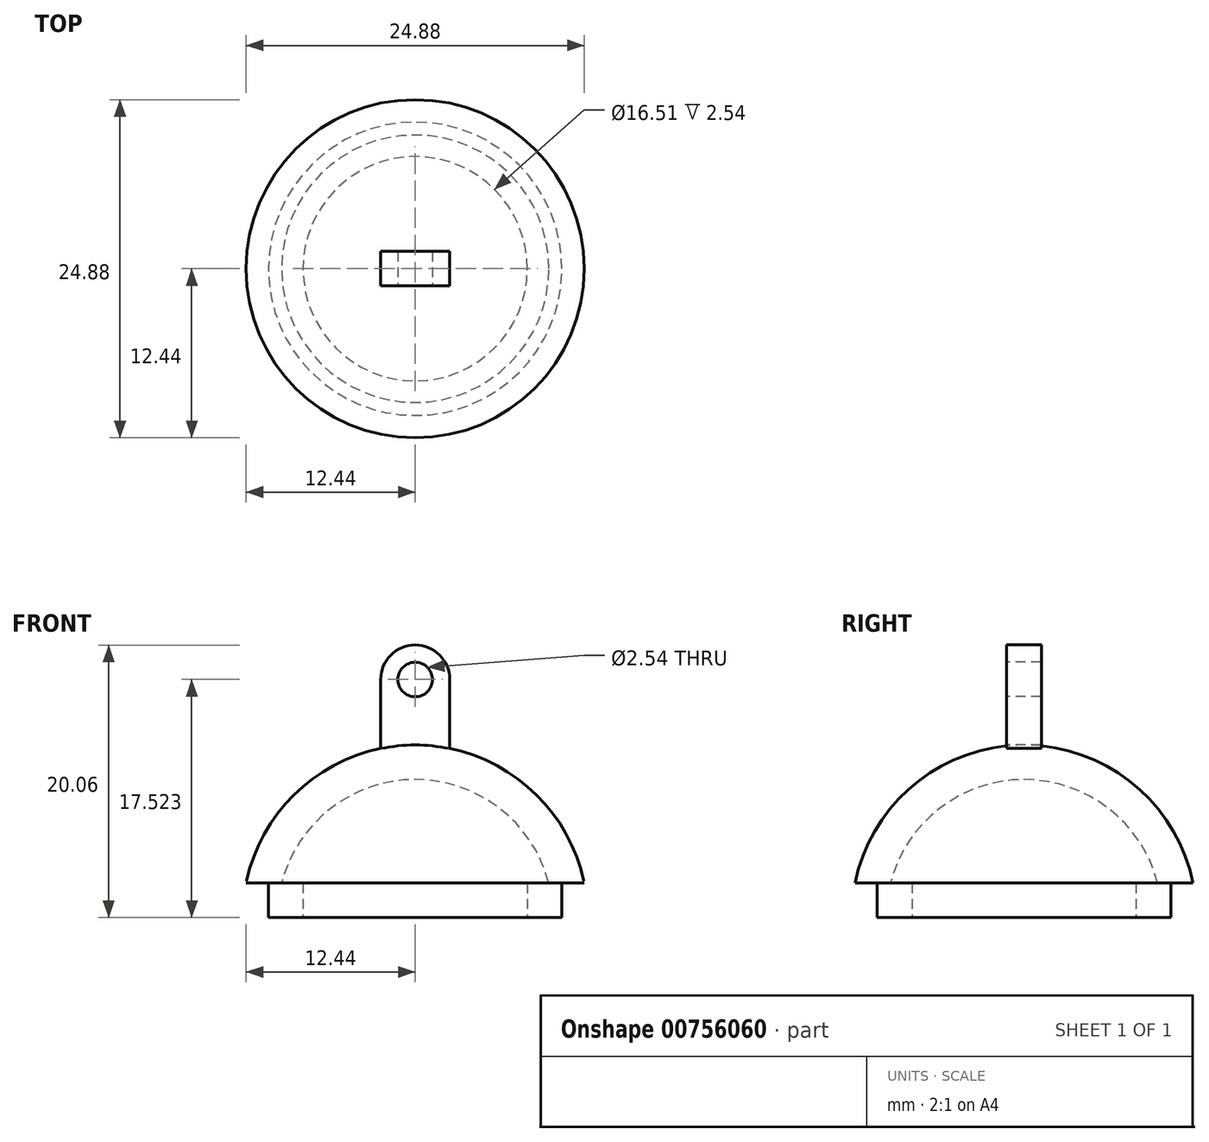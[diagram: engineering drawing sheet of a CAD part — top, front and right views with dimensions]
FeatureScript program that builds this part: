
annotation { "Feature Type Name" : "Feature", "Feature Type Description" : "" }
export const myFeature = defineFeature(function(context is Context, id is Id, definition is map)
    precondition{}
    {
        {
            var Q0;
            Q0=qCreatedBy(makeId("Top.planeOp"),FACE);
            var sketch = newSketch(context, id + "F0", { "sketchPlane" : qUnion([Q0])});
            skArc(sketch, "E0", {"start": v(12.7, 0) * mm, "mid": v(0, 12.7) * mm, "end": v(-12.7, 0) * mm});
            skLineSegment(sketch, "E1", {"start": v(-12.7, 0) * mm, "end": v(12.7, 0) * mm});
            skSolve(sketch);
        }
        {
            var Q0;
            Q0=makeQuery(id+"F0.imprint","IMPRINT",FACE,{"disambiguationData":[TD([[makeQuery(id+"F0.imprint","IMPRINT",EDGE,{"derivedFrom":sQuery(id+"F0.wireOp",EDGE,"E0")}),1.0]])]});
            var Q1;
            Q1=sQuery(id+"F0.wireOp",EDGE,"E1");
            revolve(context, id + "F1", {"surfaceOperationType" : NewSurfaceOperationType.NEW, "entities" : qUnion([Q0]), "axis" : qUnion([Q1]), "revolveType" : RevolveType.ONE_DIRECTION, "angle" : 180 * degree});
        }
        {
            var Q0;
            Q0=makeQuery(id+"F1.opRevolve","CAP_FACE",FACE,{"disambiguationData":[OSD([sQuery(id+"F0.wireOp",EDGE,"E0"),sQuery(id+"F0.wireOp",EDGE,"E1")])],"isStart":true});
            var sketch = newSketch(context, id + "F2", { "sketchPlane" : qUnion([Q0])});
            skCircle(sketch, "E2", {"center": v(0, 0) * mm, "radius": 12.7 * mm});
            skCircle(sketch, "E3", {"center": v(0, 0) * mm, "radius": 10.8 * mm});
            skSolve(sketch);
        }
        {
            var Q0;
            Q0=makeQuery(id+"F2.imprint","IMPRINT",FACE,{"disambiguationData":[TD([[makeQuery(id+"F2.imprint","IMPRINT",EDGE,{"derivedFrom":sQuery(id+"F2.wireOp",EDGE,"E2")}),1.0]])]});
            extrude(context, id + "F3", {"entities" : qUnion([Q0]), "operationType" : NewBodyOperationType.REMOVE, "oppositeDirection" : true, "depth" : 2.54 * mm, "offsetDistance" : 25.4 * mm});
        }
        {
            var Q0;
            Q0=makeQuery(id+"F3.boolean.opBoolean","COPY",FACE,{"derivedFrom":makeQuery(id+"F3.opExtrude","CAP_FACE",FACE,{"disambiguationData":[OSD([sQuery(id+"F2.wireOp",EDGE,"E2")])],"isStart":false})});
            var Q1;
            Q1=makeQuery(id+"F1.opRevolve","CAP_FACE",FACE,{"disambiguationData":[OSD([sQuery(id+"F0.wireOp",EDGE,"E0"),sQuery(id+"F0.wireOp",EDGE,"E1")])],"isStart":true});
            shell(context, id + "F4", {"entities" : qUnion([Q0, Q1]), "thickness" : 2.54 * mm});
        }
        {
            var Q0;
            Q0=qCreatedBy(makeId("Front.planeOp"),FACE);
            var sketch = newSketch(context, id + "F5", { "sketchPlane" : qUnion([Q0])});
            skLineSegment(sketch, "E4", {"start": v(-2.54, 12.44) * mm, "end": v(-2.54, 17.52) * mm});
            skLineSegment(sketch, "E5", {"start": v(2.54, 12.44) * mm, "end": v(2.54, 17.52) * mm});
            skArc(sketch, "E6", {"start": v(2.54, 12.44) * mm, "mid": v(0, 12.7) * mm, "end": v(-2.54, 12.44) * mm});
            skArc(sketch, "E7", {"start": v(2.54, 17.52) * mm, "mid": v(0, 20.06) * mm, "end": v(-2.54, 17.52) * mm});
            skCircle(sketch, "E8", {"center": v(0, 17.52) * mm, "radius": 1.27 * mm});
            skSolve(sketch);
        }
        {
            var Q0;
            Q0=makeQuery(id+"F5.imprint","IMPRINT",FACE,{"disambiguationData":[TD([[makeQuery(id+"F5.imprint","IMPRINT",EDGE,{"derivedFrom":sQuery(id+"F5.wireOp",EDGE,"E4")}),-1.0]])]});
            extrude(context, id + "F6", {"entities" : qUnion([Q0]), "oppositeDirection" : true, "depth" : 1.27 * mm, "offsetDistance" : 25.4 * mm});
        }
        {
            var Q0;
            Q0=qCreatedBy(makeId("Front.planeOp"),FACE);
            var sketch = newSketch(context, id + "F7", { "sketchPlane" : qUnion([Q0])});
            skArc(sketch, "E9", {"start": v(2.54, 12.44) * mm, "mid": v(0, 12.7) * mm, "end": v(-2.54, 12.44) * mm});
            skLineSegment(sketch, "E10", {"start": v(-2.54, 12.44) * mm, "end": v(-2.54, 17.52) * mm});
            skLineSegment(sketch, "E11", {"start": v(2.54, 12.44) * mm, "end": v(2.54, 17.52) * mm});
            skArc(sketch, "E12", {"start": v(2.54, 17.52) * mm, "mid": v(0, 20.06) * mm, "end": v(-2.54, 17.52) * mm});
            skCircle(sketch, "E13", {"center": v(0, 17.52) * mm, "radius": 1.27 * mm});
            skSolve(sketch);
        }
        {
            var Q0;
            Q0=makeQuery(id+"F7.imprint","IMPRINT",FACE,{"disambiguationData":[TD([[makeQuery(id+"F7.imprint","IMPRINT",EDGE,{"derivedFrom":sQuery(id+"F7.wireOp",EDGE,"E9")}),-1.0]])]});
            extrude(context, id + "F8", {"entities" : qUnion([Q0]), "operationType" : NewBodyOperationType.ADD, "depth" : 1.27 * mm, "offsetDistance" : 25.4 * mm});
        }
    });
